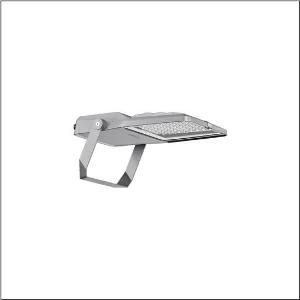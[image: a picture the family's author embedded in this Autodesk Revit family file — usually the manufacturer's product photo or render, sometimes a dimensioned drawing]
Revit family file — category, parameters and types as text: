
# Revit family: floodlight_fl_21_iq_mini___pl33t_5xa7772c1f1a_9de6
name_source: partatom
category: Lighting Fixtures
units: mm (PartAtom-declared; Revit-internal decimal feet)

## family parameters
Cut with Voids When Loaded = No
Host = Face
Light Source = No
Part Type = Normal
Room Calculation Point = No
Round Connector Dimension = Use Diameter
Shared = No

## types (1)
- --- (1 x LED, 10000 lm, 87.2 W, 2200K)
    Apparent Load = 87 VA
    CIE Flux Codes = 26 75 99 100 100
    Color Rendering = 70
    Color Temperature = 2200K
    Default Elevation = 1800 mm
    Description = Floodlight FL 21 iQ mini, floodlight, primary light control with lens, of PMMA, primary optical cover: protective disc, of toughened safety glass, transparent, light distribution: PL33T, light emission: direct distribution, installation type: surface-mounted, LED, High Power LED, rated luminous flux: 10.000lm, luminous efficacy: 115lm/W, light colour: 722, colour temperature: 2200K, control: Street-Remote, Auto-Match, Temp-Guard, Night-Set, Smart-Wire, Desk-Remote (wireless, voltage-free reading and setting of iQ features in the workshop via application-optimized NFC function/RFID function), optimised constant luminous flux control (CLO 2.0), with terminal, 6-pole, mains connection: 220..240V, AC, 50/60Hz, start of lifetime: 87W, end of service life: 92W, reduction: 40W, luminaire housing, of diecast aluminium, powder-coated, Siteco® metallic grey (DB 702S), corrosivity category C5 mid according to DIN EN ISO 12944, sealing non-destructively replaceable, mounting bracket, of steel, galvanised, powder-coated, Siteco® metallic grey (DB 702S), protection rating (complete): IP66, insulation class (complete): insulation class II (safety insulation), certification: CE, ENEC, VDE, protection symbol: D, impact resistance: IK08, permissible operating ambient temperature: -40..+40°C, permissible operating ambient temperature for outdoor applications: -40..+50°C, standard: DIN EN 12944, LABS conformity tested according to VDMA 24364:2018-05, packaging unit: 1 piece

Light Distribution: PL33T
    Height = 70 mm
    Lamp = 1 x LED
    Lamp Light Flux = 10000 lm
    Lamp Power = 87.2 W
    Lamp count = 1
    Length = 485 mm
    Luminous efficacy = 115 lm/W
    Manufacturer = Siteco
    ModVariant = No
    Model = 5XA7772C1F1A
    Number of Poles = 1
    OnlyDefault = Yes
    Power Factor = 1
    Product Name = Floodlight FL 21 iQ mini | PL33T
    Product group = floodlight | pylon annexe
    ProductGroupID = 6200
    Protection Class = Protection class II
    Protection Degree = IP 66
    RLX_Detail_Level = 1
    RLX_Emergency_Light_Flux = 0 lm
    RLX_Emergency_Type = 0
    RLX_Emergency_Type_DB = No
    RlxData = <blob elided: 96037 chars, md5=8715a0b0>
    Socket = socket
    Standby Power = 0 W
    System Light Flux = 10000 lm
    System Power = 87 W
    Type Comments = factory setting: luminous flux: 100 % | dim-lin: 254 | 456 mA
    Type Image = l_1006845.jpg
    URL = http://relux.com
    VarID = @adj_082083
    Voltage = 0 V
    Weight = 0.00 kg
    Width = 337 mm

## geometry (parser evidence)
native form markers: Blend x4, Sweep x11
no freeform markers — native parametric forms only
